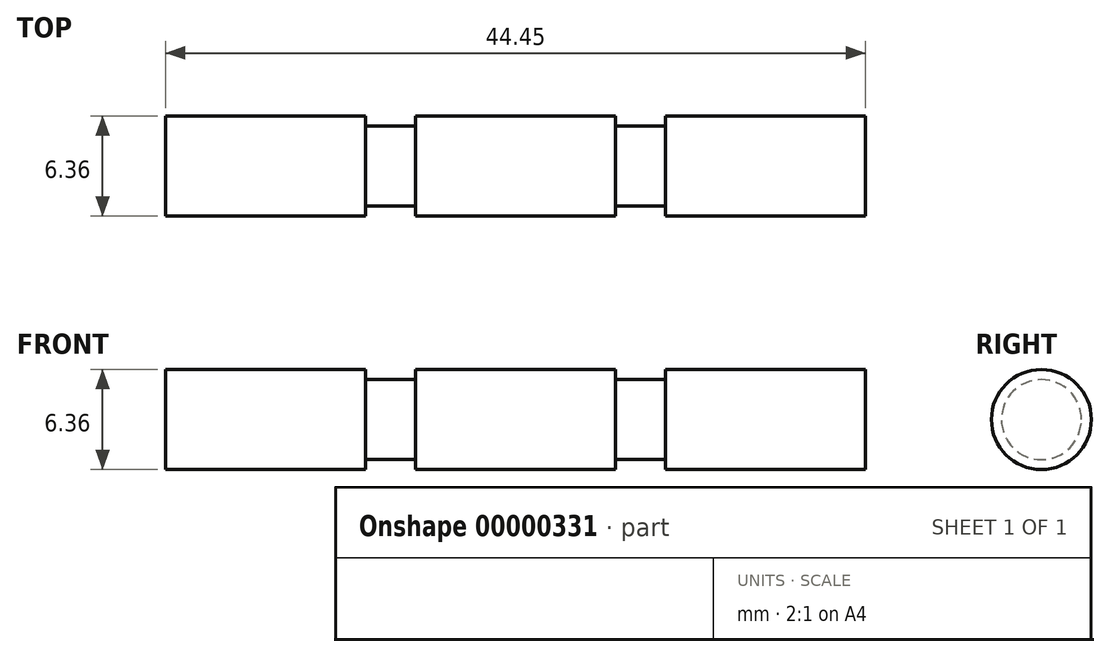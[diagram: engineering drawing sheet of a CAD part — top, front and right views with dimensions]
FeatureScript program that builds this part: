
annotation { "Feature Type Name" : "Feature", "Feature Type Description" : "" }
export const myFeature = defineFeature(function(context is Context, id is Id, definition is map)
    precondition{}
    {
        {
            var Q0;
            Q0=qCreatedBy(makeId("Top.planeOp"),FACE);
            var sketch = newSketch(context, id + "F0", { "sketchPlane" : qUnion([Q0])});
            skLineSegment(sketch, "E0", {"start": v(0, 0) * mm, "end": v(0, 3.18) * mm});
            skLineSegment(sketch, "E1", {"start": v(0, 3.18) * mm, "end": v(12.7, 3.18) * mm});
            skLineSegment(sketch, "E2", {"start": v(12.7, 3.18) * mm, "end": v(12.7, 2.54) * mm});
            skLineSegment(sketch, "E3", {"start": v(12.7, 2.54) * mm, "end": v(15.88, 2.54) * mm});
            skLineSegment(sketch, "E4", {"start": v(15.88, 2.54) * mm, "end": v(15.88, 3.18) * mm});
            skLineSegment(sketch, "E5", {"start": v(15.88, 3.18) * mm, "end": v(28.58, 3.18) * mm});
            skLineSegment(sketch, "E6", {"start": v(28.58, 3.17) * mm, "end": v(28.58, 2.54) * mm});
            skLineSegment(sketch, "E7", {"start": v(28.58, 2.54) * mm, "end": v(31.75, 2.54) * mm});
            skLineSegment(sketch, "E8", {"start": v(31.75, 2.54) * mm, "end": v(31.75, 3.17) * mm});
            skLineSegment(sketch, "E9", {"start": v(31.75, 3.18) * mm, "end": v(44.45, 3.18) * mm});
            skLineSegment(sketch, "E10", {"start": v(44.45, 3.18) * mm, "end": v(44.45, 0) * mm});
            skLineSegment(sketch, "E11", {"start": v(44.45, 0) * mm, "end": v(0, 0) * mm});
            skSolve(sketch);
        }
        {
            var Q0;
            Q0=makeQuery(id+"F0.imprint","IMPRINT",FACE,{"disambiguationData":[TD([[makeQuery(id+"F0.imprint","IMPRINT",EDGE,{"derivedFrom":sQuery(id+"F0.wireOp",EDGE,"E0")}),-1.0]])]});
            var Q1;
            Q1=sQuery(id+"F0.wireOp",EDGE,"E11");
            revolve(context, id + "F1", {"entities" : qUnion([Q0]), "axis" : qUnion([Q1]), "revolveType" : RevolveType.FULL});
        }
    });
